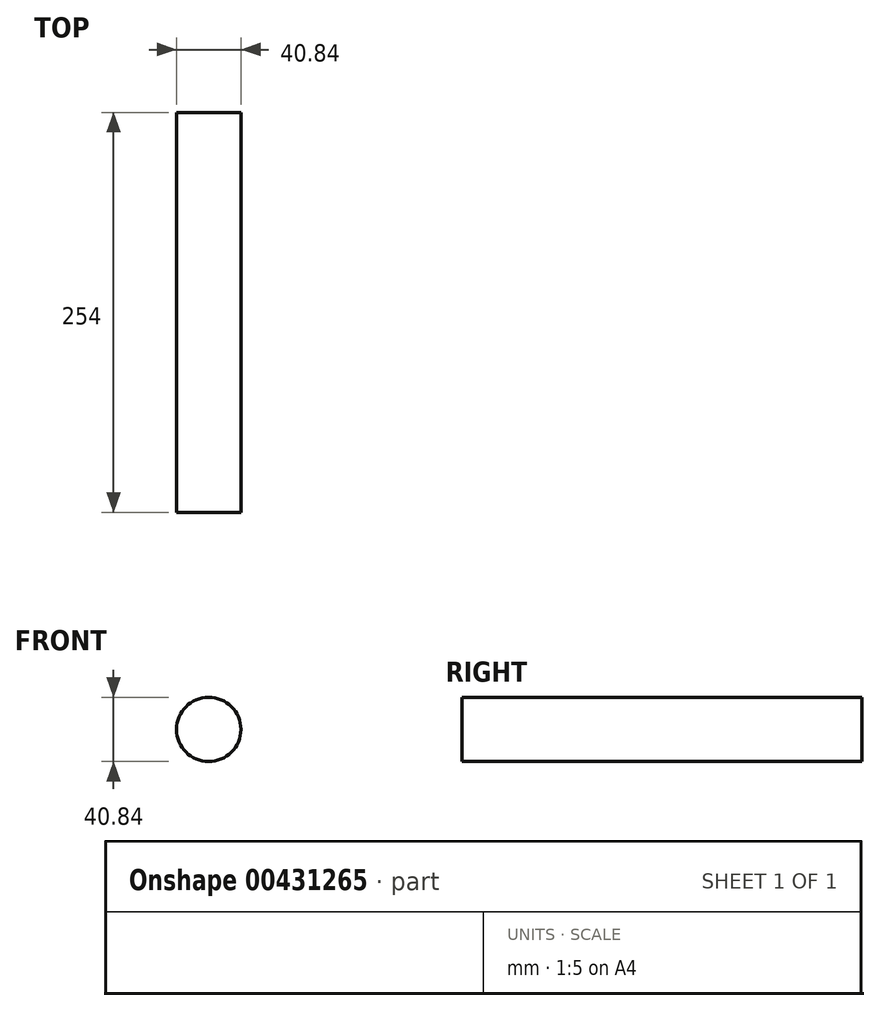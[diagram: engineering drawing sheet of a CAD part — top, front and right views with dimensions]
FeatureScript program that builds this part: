
annotation { "Feature Type Name" : "Feature", "Feature Type Description" : "" }
export const myFeature = defineFeature(function(context is Context, id is Id, definition is map)
    precondition{}
    {
        {
            var Q0;
            Q0=qCreatedBy(makeId("Front.planeOp"),FACE);
            var sketch = newSketch(context, id + "F0", { "sketchPlane" : qUnion([Q0])});
            skCircle(sketch, "E0", {"center": v(0, 0) * mm, "radius": 20.42 * mm});
            skSolve(sketch);
        }
        {
            var Q0;
            Q0 = qSketchRegion(id + "F0", true);
            extrude(context, id + "F1", {"entities" : qUnion([Q0]), "depth" : 254 * mm});
        }
    });
